# Revit family: DS3B
name_source: partatom
category: Generic Models
revit_build: Autodesk Revit LT 2017 (Build: 20160225_1515(x64)
units: mm (PartAtom-declared; Revit-internal decimal feet)

## family parameters
Always vertical = No
Can host rebar = No
Cut with Voids When Loaded = No
Part Type = Normal
Room Calculation Point = No
Round Connector Dimension = Use Diameter
Shared = No
Work Plane-Based = Yes

## types (1)
- NBS Standard Parameters
    BIMObjectName = Metpro_metprolibrary_conduitfittings_metalcomponent_steelaccessories
    Default Elevation = 1219 mm
    Description = DS3B - 32mm Distance Saddle
    DurationUnit = year
    Finish = Black
    Keynote = Comprises of Body, Strap & 2 Screws
    ManufacturerName = Metpro Ltd
    ManufacturerURL = www.metpro.co.uk
    Material = Cast  Body, Pressed Steel Strap
    ModelReference = DS3B
    NBSDescription = Conduit Fittings
    NBSReference = 90-55-10/460
    NominalHeight = 39 mm  [stored 0.127953 ft]
    NominalLength = 73 mm
    NominalWidth = 22 mm  [stored 0.0721785 ft]
    ProductInformation = www.metpro.co.uk/pdf/ds3g.pdf
    Size = 32mm
    Uniclass2 = PR_65_70_11_20
    Version = 1
    WarrantyDurationUnit = year
    Weight = 0.128Kg

note: [stored X ft] marks values corroborated as IEEE doubles in the binary element streams (Revit-internal decimal feet)

## geometry (parser evidence)
native form markers: Sweep x2
no freeform markers — native parametric forms only
